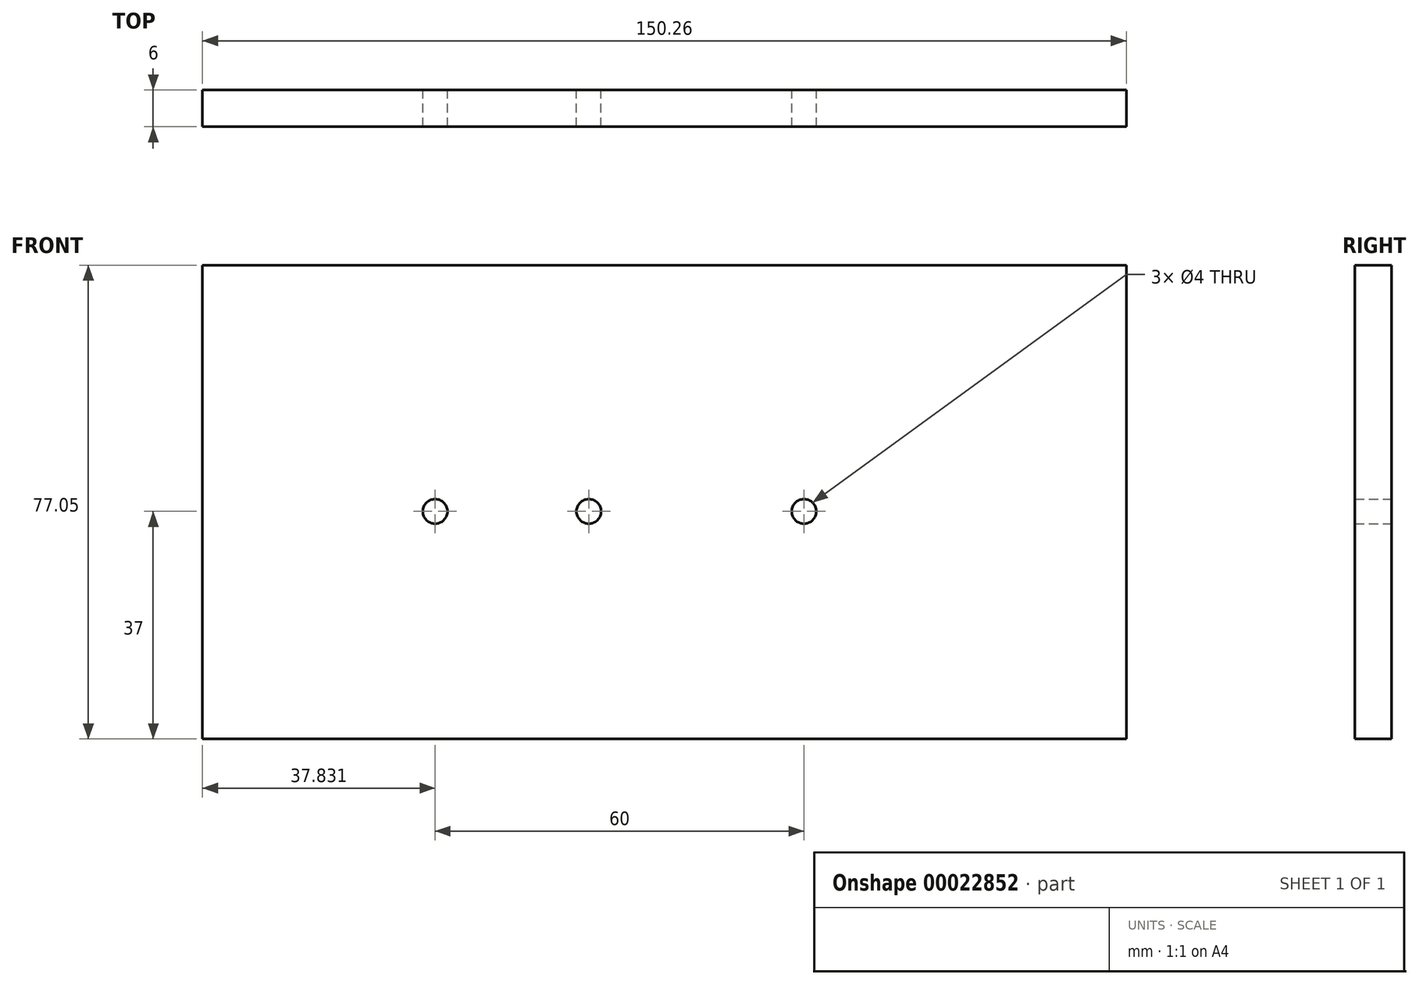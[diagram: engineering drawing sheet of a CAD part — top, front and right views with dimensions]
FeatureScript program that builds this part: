
annotation { "Feature Type Name" : "Feature", "Feature Type Description" : "" }
export const myFeature = defineFeature(function(context is Context, id is Id, definition is map)
    precondition{}
    {
        {
            var Q0;
            Q0=qCreatedBy(makeId("Front.planeOp"),FACE);
            var sketch = newSketch(context, id + "F0", { "sketchPlane" : qUnion([Q0])});
            skLineSegment(sketch, "E0.bottom", {"start": v(-94.2, 47.3) * mm, "end": v(56.07, 47.3) * mm});
            skLineSegment(sketch, "E0.top", {"start": v(-94.2, -29.75) * mm, "end": v(56.07, -29.75) * mm});
            skLineSegment(sketch, "E0.left", {"start": v(-94.2, 47.3) * mm, "end": v(-94.2, -29.75) * mm});
            skLineSegment(sketch, "E0.right", {"start": v(56.07, 47.3) * mm, "end": v(56.07, -29.75) * mm});
            skCircle(sketch, "E1", {"center": v(-56.36, 7.25) * mm, "radius": 2 * mm});
            skCircle(sketch, "E2", {"center": v(-31.36, 7.25) * mm, "radius": 2 * mm});
            skCircle(sketch, "E3", {"center": v(3.64, 7.25) * mm, "radius": 2 * mm});
            skSolve(sketch);
        }
        {
            var Q0;
            Q0=makeQuery(id+"F0.imprint","IMPRINT",FACE,{"disambiguationData":[TD([[makeQuery(id+"F0.imprint","IMPRINT",EDGE,{"derivedFrom":sQuery(id+"F0.wireOp",EDGE,"E0.bottom")}),-1.0]])]});
            extrude(context, id + "F1", {"entities" : qUnion([Q0]), "depth" : 6 * mm});
        }
    });
